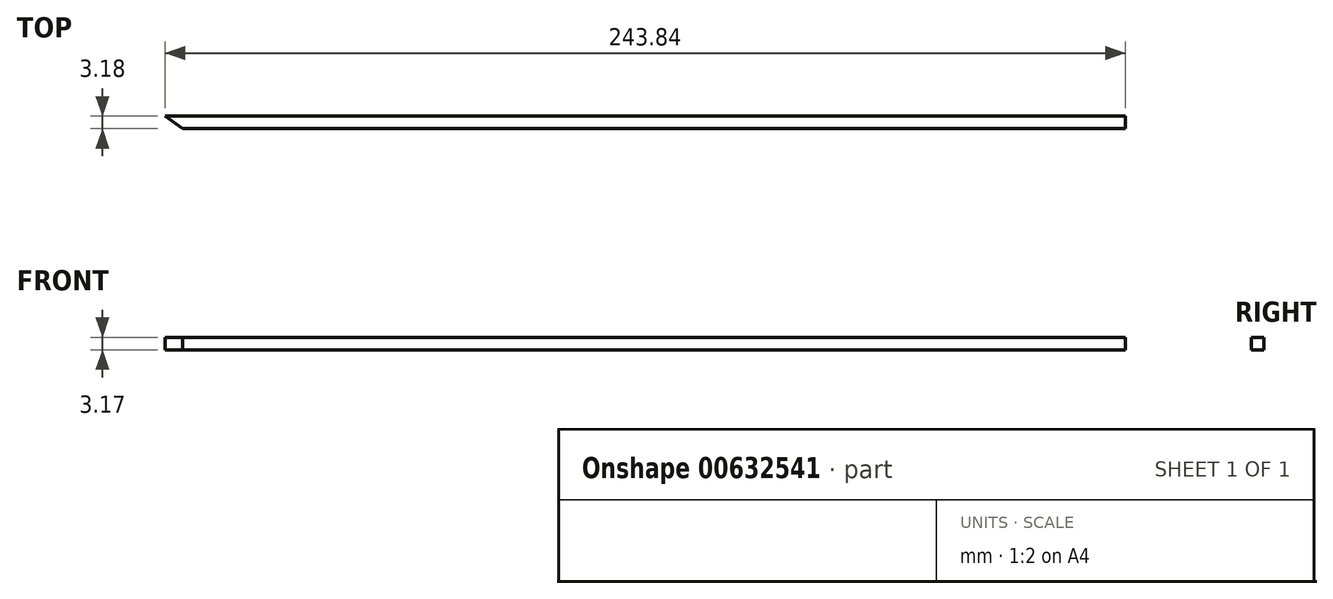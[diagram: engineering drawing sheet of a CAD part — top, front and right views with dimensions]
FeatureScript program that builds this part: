
annotation { "Feature Type Name" : "Feature", "Feature Type Description" : "" }
export const myFeature = defineFeature(function(context is Context, id is Id, definition is map)
    precondition{}
    {
        {
            var Q0;
            Q0=qCreatedBy(makeId("Top.planeOp"),FACE);
            var sketch = newSketch(context, id + "F0", { "sketchPlane" : qUnion([Q0])});
            skLineSegment(sketch, "E0", {"start": v(-147.36, 11.02) * mm, "end": v(96.48, 11.02) * mm});
            skLineSegment(sketch, "E1", {"start": v(96.48, 11.02) * mm, "end": v(96.48, 7.84) * mm});
            skLineSegment(sketch, "E2", {"start": v(96.48, 7.84) * mm, "end": v(-142.94, 7.84) * mm});
            skLineSegment(sketch, "E3", {"start": v(-142.94, 7.84) * mm, "end": v(-147.36, 11.02) * mm});
            skSolve(sketch);
        }
        {
            var Q0;
            Q0=makeQuery(id+"F0.imprint","IMPRINT",FACE,{"disambiguationData":[TD([[makeQuery(id+"F0.imprint","IMPRINT",EDGE,{"derivedFrom":sQuery(id+"F0.wireOp",EDGE,"E0")}),-1.0]])]});
            extrude(context, id + "F1", {"entities" : qUnion([Q0]), "depth" : 3.17 * mm, "offsetDistance" : 25.4 * mm});
        }
    });
